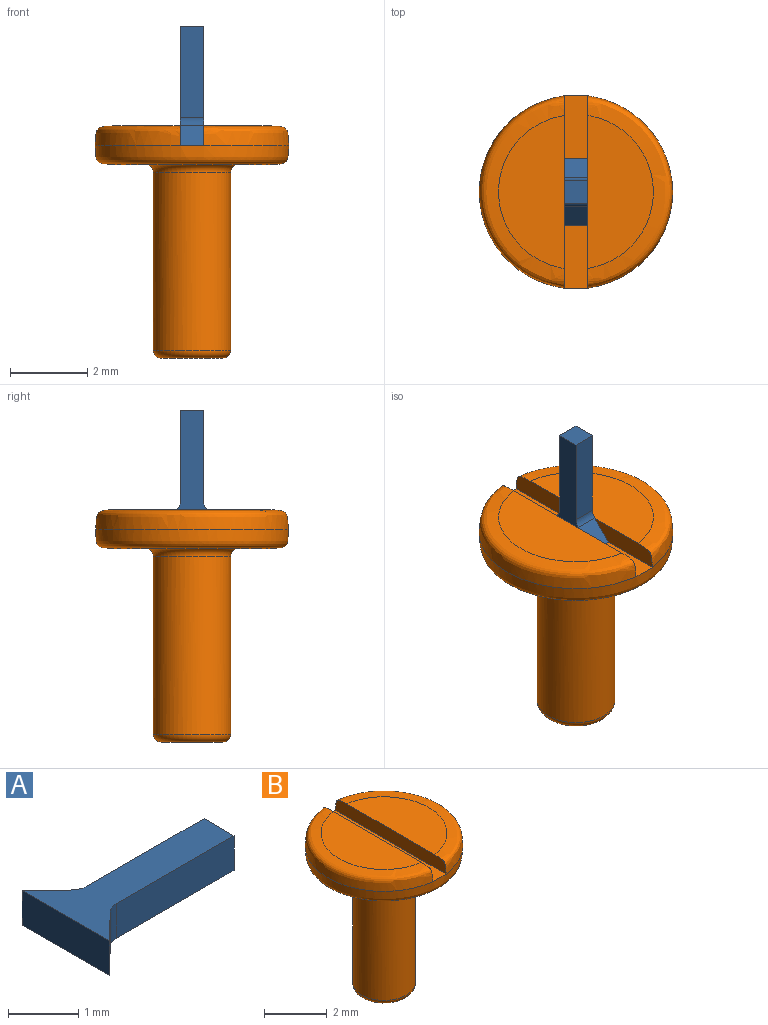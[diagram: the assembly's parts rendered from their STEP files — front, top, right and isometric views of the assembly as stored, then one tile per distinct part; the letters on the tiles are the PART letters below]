
ASSEMBLY  parts=2 mates=1
PART A: 10 faces, bbox 3.1x1.8x0.6 mm
  f0: plane 0.6x0.6mm, normal (1,0,0), area 0.4mm2, adj f1,f7,f8,f9
  f1: plane 2.36x0.6mm, normal (0,1,0), area 1.4mm2, adj f0,f2,f8,f9
  f2: cylinder r=0.3mm len=0.6mm, axis (0,0,-1), area 0.1mm2, adj f1,f3,f8,f9
  f3: plane 0.6x0.51mm, normal (0.69,0.72,0), area 0.4mm2, adj f2,f4,f8,f9
  f4: plane 1.75x0.6mm, normal (-1,0,0), area 1.1mm2, adj f3,f5,f8,f9
  f5: plane 0.6x0.51mm, normal (0.69,-0.72,0), area 0.4mm2, adj f4,f6,f8,f9
  f6: cylinder r=0.3mm len=0.6mm, axis (0,0,-1), area 0.1mm2, adj f5,f7,f8,f9
  f7: plane 2.36x0.6mm, normal (0,-1,0), area 1.4mm2, adj f0,f6,f8,f9
  f8: plane 3.08x1.75mm, normal (0,0,1), area 2.2mm2, adj f0,f1,f2,f3,f4,f5,f6,f7
  f9: plane 3.08x1.75mm, normal (0,0,-1), area 2.2mm2, adj f0,f1,f2,f3,f4,f5,f6,f7
PART B: 13 faces, bbox 5.2x5.2x6.2 mm
  f0: plane 3.99x1.72mm, normal (0,0,1), area 5.1mm2, adj f1,f10
  f1: bspline ~4.96x2.26mm, area 5.9mm2, adj f0,f4,f10
  f2: plane 4.01x4.01mm, normal (0,0,-1), area 8mm2, adj f4,f8
  f3: plane 3.99x1.72mm, normal (0,0,1), area 5.1mm2, adj f5,f11
  f4: bspline ~5x5mm, area 13mm2, adj f1,f2,f5,f12
  f5: bspline ~5x3.15mm, area 5.9mm2, adj f3,f4,f11
  f6: cylinder r=1mm len=4.6mm, axis (0,0,1), area 28.9mm2, adj f8,f9
  f7: plane 1.6x1.6mm, normal (0,0,-1), area 2mm2, adj f9
  f8: torus R=1.2mm, axis (0,0,1), area 2.1mm2, adj f2,f6
  f9: torus R=0.8mm, axis (0,0,-1), area 1.8mm2, adj f6,f7
  f10: plane 5.19x0.71mm, normal (-1,0,0), area 2.4mm2, adj f0,f1,f12
  f11: plane 5.19x0.7mm, normal (1,0,0), area 2.4mm2, adj f3,f5,f12
  f12: plane 5.04x0.64mm, normal (0,0,1), area 3mm2, adj f4,f10,f11
PLACE A rot(axis=(0,-1,0),90deg) t=(0,0,1.4)mm
PLACE B at identity fixed
MATE planar B.f6 <-> A.f4  axis (0,0,1) through (0,0,-0.5)mm
